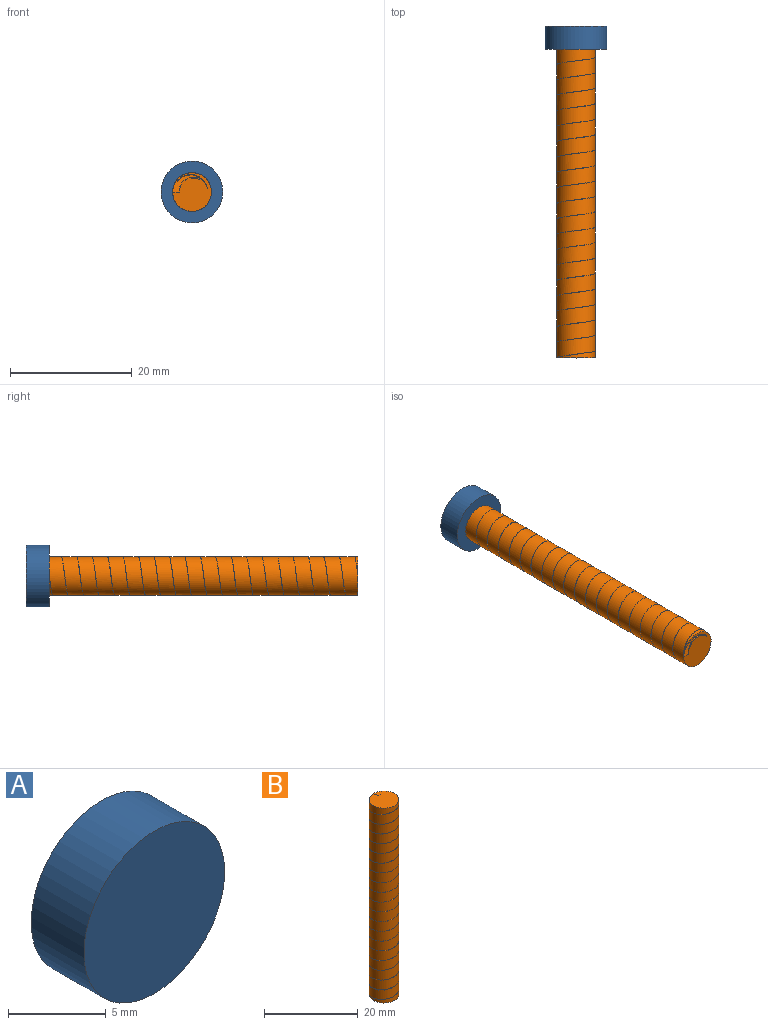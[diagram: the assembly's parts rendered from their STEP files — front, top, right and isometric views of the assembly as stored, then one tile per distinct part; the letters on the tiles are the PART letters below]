
ASSEMBLY  parts=2 mates=1
PART A: 16 faces, bbox 10.2x3.8x10.2 mm
  f0: plane 10.16x10.16mm, normal (0,1,0), area 68.7mm2, adj f1,f3,f4,f5,f6,f7,f8,f9
  f1: cylinder r=5.08mm len=10.16mm, axis (0,1,0), area 121.6mm2, adj f0,f2
  f2: plane 10.16x10.16mm, normal (0,-1,0), area 81.1mm2, adj f1
  f3: plane 2.12x1.27mm, normal (0,0,1), area 2.7mm2, adj f0,f4,f14,f15
  f4: plane 2.12x1.27mm, normal (1,0,0), area 2.7mm2, adj f0,f3,f5,f15
  f5: plane 1.27x1.27mm, normal (0,0,1), area 1.6mm2, adj f0,f4,f6,f15
  f6: plane 2.12x1.27mm, normal (-1,0,0), area 2.7mm2, adj f0,f5,f7,f15
  f7: plane 2.12x1.27mm, normal (0,0,1), area 2.7mm2, adj f0,f6,f8,f15
  f8: plane 1.27x1.27mm, normal (-1,0,0), area 1.6mm2, adj f0,f7,f9,f15
  f9: plane 2.12x1.27mm, normal (0,0,-1), area 2.7mm2, adj f0,f8,f10,f15
  f10: plane 2.12x1.27mm, normal (-1,0,0), area 2.7mm2, adj f0,f9,f11,f15
  f11: plane 1.27x1.27mm, normal (0,0,-1), area 1.6mm2, adj f0,f10,f12,f15
  f12: plane 2.12x1.27mm, normal (1,0,0), area 2.7mm2, adj f0,f11,f13,f15
  f13: plane 2.12x1.27mm, normal (0,0,-1), area 2.7mm2, adj f0,f12,f14,f15
  f14: plane 1.27x1.27mm, normal (1,0,0), area 1.6mm2, adj f0,f3,f13,f15
  f15: plane 5.52x5.52mm, normal (0,1,0), area 12.4mm2, adj f3,f4,f5,f6,f7,f8,f9,f10
PART B: 8 faces, bbox 7.7x6.7x52.2 mm
  f0: plane 6.35x6.35mm, normal (0,0,1), area 31.6mm2, adj f1,f3,f5,f6
  f1: cylinder r=3.17mm len=50.8mm, axis (0,0,-1), area 988.9mm2, adj f0,f2,f3,f4,f6,f7
  f2: plane 6.71x6.71mm, normal (0,0,-1), area 28.1mm2, adj f1,f4,f5,f7
  f3: plane 1.12x0.98mm, normal (1,0,0), area 0.6mm2, adj f0,f1,f5,f7
  f4: plane 1.13x0.02mm, normal (-1,0,0), area 0mm2, adj f1,f2,f5,f6
  f5: bspline ~51.8x6.01mm, area 330.1mm2, adj f0,f2,f3,f4,f6,f7
  f6: bspline ~50.82x7.37mm, area 371.7mm2, adj f0,f1,f4,f5
  f7: bspline ~51.78x7.37mm, area 399.2mm2, adj f1,f2,f3,f5
PLACE A t=(9.94,15.74,12.15)mm
PLACE B rot(axis=(-0.58,0.58,0.58),120deg) t=(9.94,-38.87,12.15)mm
MATE fastened B.f1 <-> A.f1  axis (0,1,0) through (9.94,11.93,12.15)mm
